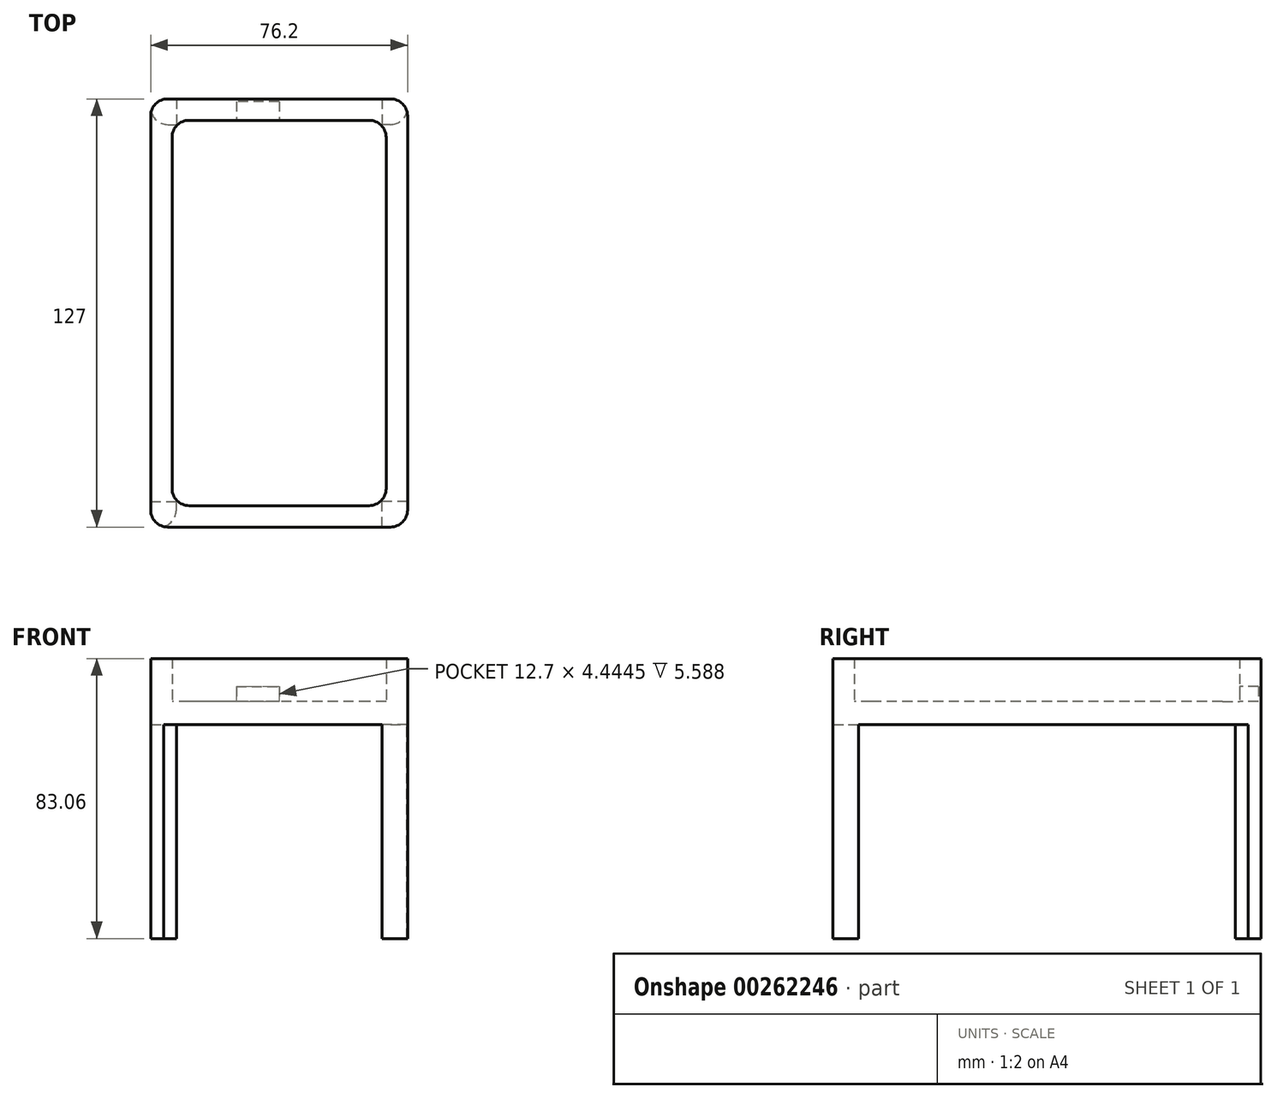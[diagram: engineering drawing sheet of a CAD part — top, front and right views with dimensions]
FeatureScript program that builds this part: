
annotation { "Feature Type Name" : "Feature", "Feature Type Description" : "" }
export const myFeature = defineFeature(function(context is Context, id is Id, definition is map)
    precondition{}
    {
        {
            var Q0;
            Q0=qCreatedBy(makeId("Top.planeOp"),FACE);
            var sketch = newSketch(context, id + "F0", { "sketchPlane" : qUnion([Q0])});
            skLineSegment(sketch, "E0.bottom", {"start": v(38.1, 63.5) * mm, "end": v(-38.1, 63.5) * mm});
            skLineSegment(sketch, "E0.top", {"start": v(38.1, -63.5) * mm, "end": v(-38.1, -63.5) * mm});
            skLineSegment(sketch, "E0.left", {"start": v(38.1, 63.5) * mm, "end": v(38.1, -63.5) * mm});
            skLineSegment(sketch, "E0.right", {"start": v(-38.1, 63.5) * mm, "end": v(-38.1, -63.5) * mm});
            skPoint(sketch, "E0.middle", {"position": v(0, 0) * mm});
            skLineSegment(sketch, "E1.bottom", {"start": v(31.75, 57.15) * mm, "end": v(-31.75, 57.15) * mm});
            skLineSegment(sketch, "E1.top", {"start": v(31.75, -57.15) * mm, "end": v(-31.75, -57.15) * mm});
            skLineSegment(sketch, "E1.left", {"start": v(31.75, 57.15) * mm, "end": v(31.75, -57.15) * mm});
            skLineSegment(sketch, "E1.right", {"start": v(-31.75, 57.15) * mm, "end": v(-31.75, -57.15) * mm});
            skSolve(sketch);
        }
        {
            var Q0;
            Q0 = qSketchRegion(id + "F0", true);
            extrude(context, id + "F1", {"entities" : qUnion([Q0]), "depth" : 12.7 * mm});
        }
        {
            var Q0;
            Q0=qCreatedBy(makeId("Top.planeOp"),FACE);
            var sketch = newSketch(context, id + "F2", { "sketchPlane" : qUnion([Q0])});
            skLineSegment(sketch, "E2.bottom", {"start": v(-38.1, 63.5) * mm, "end": v(38.1, 63.5) * mm});
            skLineSegment(sketch, "E2.top", {"start": v(-38.1, -63.5) * mm, "end": v(38.1, -63.5) * mm});
            skLineSegment(sketch, "E2.left", {"start": v(-38.1, 63.5) * mm, "end": v(-38.1, -63.5) * mm});
            skLineSegment(sketch, "E2.right", {"start": v(38.1, 63.5) * mm, "end": v(38.1, -63.5) * mm});
            skPoint(sketch, "E2.middle", {"position": v(0, 0) * mm});
            skSolve(sketch);
        }
        {
            var Q0;
            Q0 = qSketchRegion(id + "F2", true);
            extrude(context, id + "F3", {"entities" : qUnion([Q0]), "operationType" : NewBodyOperationType.ADD, "oppositeDirection" : true, "depth" : 6.86 * mm});
        }
        {
            var Q0;
            Q0=makeQuery(id+"F3.opExtrude","CAP_FACE",FACE,{"disambiguationData":[OSD([sQuery(id+"F2.wireOp",EDGE,"E2.bottom"),sQuery(id+"F2.wireOp",EDGE,"E2.top"),sQuery(id+"F2.wireOp",EDGE,"E2.left"),sQuery(id+"F2.wireOp",EDGE,"E2.right")])],"isStart":false});
            var sketch = newSketch(context, id + "F4", { "sketchPlane" : qUnion([Q0])});
            skLineSegment(sketch, "E3.bottom", {"start": v(38.1, -63.5) * mm, "end": v(30.48, -63.5) * mm});
            skLineSegment(sketch, "E3.top", {"start": v(38.1, -55.88) * mm, "end": v(30.48, -55.88) * mm});
            skLineSegment(sketch, "E3.left", {"start": v(38.1, -63.5) * mm, "end": v(38.1, -55.88) * mm});
            skLineSegment(sketch, "E3.right", {"start": v(30.48, -63.5) * mm, "end": v(30.48, -55.88) * mm});
            skLineSegment(sketch, "E4.MirrorCS", {"start": v(-38.1, -55.88) * mm, "end": v(-30.48, -55.88) * mm});
            skLineSegment(sketch, "E5.MirrorCS", {"start": v(-38.1, -63.5) * mm, "end": v(-38.1, -55.88) * mm});
            skLineSegment(sketch, "E6.MirrorCS", {"start": v(-38.1, -63.5) * mm, "end": v(-30.48, -63.5) * mm});
            skLineSegment(sketch, "E7.MirrorCS", {"start": v(-30.48, -63.5) * mm, "end": v(-30.48, -55.88) * mm});
            skLineSegment(sketch, "E8.MirrorCS", {"start": v(38.1, 55.88) * mm, "end": v(30.48, 55.88) * mm});
            skLineSegment(sketch, "E9.MirrorCS", {"start": v(30.48, 63.5) * mm, "end": v(30.48, 55.88) * mm});
            skLineSegment(sketch, "E10.MirrorCS", {"start": v(38.1, 63.5) * mm, "end": v(30.48, 63.5) * mm});
            skLineSegment(sketch, "E11.MirrorCS", {"start": v(38.1, 63.5) * mm, "end": v(38.1, 55.88) * mm});
            skLineSegment(sketch, "E12.MirrorCS", {"start": v(-30.48, 63.5) * mm, "end": v(-30.48, 55.88) * mm});
            skLineSegment(sketch, "E13.MirrorCS", {"start": v(-38.1, 55.88) * mm, "end": v(-30.48, 55.88) * mm});
            skLineSegment(sketch, "E14.MirrorCS", {"start": v(-38.1, 63.5) * mm, "end": v(-38.1, 55.88) * mm});
            skLineSegment(sketch, "E15.MirrorCS", {"start": v(-38.1, 63.5) * mm, "end": v(-30.48, 63.5) * mm});
            skSolve(sketch);
        }
        {
            var Q0;
            Q0=makeQuery(id+"F4.imprint","IMPRINT",FACE,{"disambiguationData":[TD([[makeQuery(id+"F4.imprint","IMPRINT",EDGE,{"derivedFrom":sQuery(id+"F4.wireOp",EDGE,"E3.bottom")}),1.0]])]});
            var Q1;
            Q1=makeQuery(id+"F4.imprint","IMPRINT",FACE,{"disambiguationData":[TD([[makeQuery(id+"F4.imprint","IMPRINT",EDGE,{"derivedFrom":sQuery(id+"F4.wireOp",EDGE,"E8.MirrorCS")}),-1.0]])]});
            var Q2;
            Q2=makeQuery(id+"F4.imprint","IMPRINT",FACE,{"disambiguationData":[TD([[makeQuery(id+"F4.imprint","IMPRINT",EDGE,{"derivedFrom":sQuery(id+"F4.wireOp",EDGE,"E12.MirrorCS")}),-1.0]])]});
            var Q3;
            Q3=makeQuery(id+"F4.imprint","IMPRINT",FACE,{"disambiguationData":[TD([[makeQuery(id+"F4.imprint","IMPRINT",EDGE,{"derivedFrom":sQuery(id+"F4.wireOp",EDGE,"E4.MirrorCS")}),-1.0]])]});
            extrude(context, id + "F5", {"entities" : qUnion([Q0, Q1, Q2, Q3]), "operationType" : NewBodyOperationType.ADD, "depth" : 63.5 * mm});
        }
        {
            var Q0;
            Q0=makeQuery(id+"F5.boolean.opBoolean","MERGE",EDGE,{"derivedFrom":[makeQuery(id+"F3.boolean.opBoolean","MERGE",EDGE,{"derivedFrom":[makeQuery(id+"F1.opExtrude","SWEPT_EDGE",EDGE,{"disambiguationData":[OSD([sQuery(id+"F0.wireOp",EDGE,"E0.top"),sQuery(id+"F0.wireOp",EDGE,"E0.left")])]}),makeQuery(id+"F3.opExtrude","SWEPT_EDGE",EDGE,{"disambiguationData":[OSD([sQuery(id+"F2.wireOp",EDGE,"E2.top"),sQuery(id+"F2.wireOp",EDGE,"E2.right")])]})]}),makeQuery(id+"F5.opExtrude","SWEPT_EDGE",EDGE,{"disambiguationData":[OSD([sQuery(id+"F4.wireOp",EDGE,"E10.MirrorCS"),sQuery(id+"F4.wireOp",EDGE,"E11.MirrorCS")])]})]});
            var Q1;
            Q1=makeQuery(id+"F5.boolean.opBoolean","MERGE",EDGE,{"derivedFrom":[makeQuery(id+"F3.boolean.opBoolean","MERGE",EDGE,{"derivedFrom":[makeQuery(id+"F1.opExtrude","SWEPT_EDGE",EDGE,{"disambiguationData":[OSD([sQuery(id+"F0.wireOp",EDGE,"E0.bottom"),sQuery(id+"F0.wireOp",EDGE,"E0.left")])]}),makeQuery(id+"F3.opExtrude","SWEPT_EDGE",EDGE,{"disambiguationData":[OSD([sQuery(id+"F2.wireOp",EDGE,"E2.bottom"),sQuery(id+"F2.wireOp",EDGE,"E2.right")])]})]}),makeQuery(id+"F5.opExtrude","SWEPT_EDGE",EDGE,{"disambiguationData":[OSD([sQuery(id+"F4.wireOp",EDGE,"E3.bottom"),sQuery(id+"F4.wireOp",EDGE,"E3.left")])]})]});
            var Q2;
            Q2=makeQuery(id+"F5.opExtrude","SWEPT_EDGE",EDGE,{"disambiguationData":[OSD([sQuery(id+"F2.wireOp",EDGE,"E2.right"),sQuery(id+"F4.wireOp",EDGE,"E3.top"),sQuery(id+"F4.wireOp",EDGE,"E3.left")])]});
            var Q3;
            Q3=makeQuery(id+"F5.opExtrude","SWEPT_EDGE",EDGE,{"disambiguationData":[OSD([sQuery(id+"F2.wireOp",EDGE,"E2.top"),sQuery(id+"F4.wireOp",EDGE,"E12.MirrorCS"),sQuery(id+"F4.wireOp",EDGE,"E15.MirrorCS")])]});
            var Q4;
            Q4=makeQuery(id+"F5.boolean.opBoolean","MERGE",EDGE,{"derivedFrom":[makeQuery(id+"F3.boolean.opBoolean","MERGE",EDGE,{"derivedFrom":[makeQuery(id+"F1.opExtrude","SWEPT_EDGE",EDGE,{"disambiguationData":[OSD([sQuery(id+"F0.wireOp",EDGE,"E0.top"),sQuery(id+"F0.wireOp",EDGE,"E0.right")])]}),makeQuery(id+"F3.opExtrude","SWEPT_EDGE",EDGE,{"disambiguationData":[OSD([sQuery(id+"F2.wireOp",EDGE,"E2.top"),sQuery(id+"F2.wireOp",EDGE,"E2.left")])]})]}),makeQuery(id+"F5.opExtrude","SWEPT_EDGE",EDGE,{"disambiguationData":[OSD([sQuery(id+"F4.wireOp",EDGE,"E14.MirrorCS"),sQuery(id+"F4.wireOp",EDGE,"E15.MirrorCS")])]})]});
            var Q5;
            Q5=makeQuery(id+"F5.boolean.opBoolean","MERGE",EDGE,{"derivedFrom":[makeQuery(id+"F3.boolean.opBoolean","MERGE",EDGE,{"derivedFrom":[makeQuery(id+"F1.opExtrude","SWEPT_EDGE",EDGE,{"disambiguationData":[OSD([sQuery(id+"F0.wireOp",EDGE,"E0.bottom"),sQuery(id+"F0.wireOp",EDGE,"E0.right")])]}),makeQuery(id+"F3.opExtrude","SWEPT_EDGE",EDGE,{"disambiguationData":[OSD([sQuery(id+"F2.wireOp",EDGE,"E2.bottom"),sQuery(id+"F2.wireOp",EDGE,"E2.left")])]})]}),makeQuery(id+"F5.opExtrude","SWEPT_EDGE",EDGE,{"disambiguationData":[OSD([sQuery(id+"F4.wireOp",EDGE,"E5.MirrorCS"),sQuery(id+"F4.wireOp",EDGE,"E6.MirrorCS")])]})]});
            var Q6;
            Q6=makeQuery(id+"F5.opExtrude","SWEPT_EDGE",EDGE,{"disambiguationData":[OSD([sQuery(id+"F2.wireOp",EDGE,"E2.left"),sQuery(id+"F4.wireOp",EDGE,"E4.MirrorCS"),sQuery(id+"F4.wireOp",EDGE,"E5.MirrorCS")])]});
            fillet(context, id + "F6", {"entities" : qUnion([Q0, Q1, Q2, Q3, Q4, Q5, Q6]), "radius" : 5.08 * mm, "tangentPropagation" : true, "allowEdgeOverflow" : false});
        }
        {
            var Q0;
            Q0=makeQuery(id+"F1.opExtrude","SWEPT_EDGE",EDGE,{"disambiguationData":[OSD([sQuery(id+"F0.wireOp",EDGE,"E1.top"),sQuery(id+"F0.wireOp",EDGE,"E1.right")])]});
            var Q1;
            Q1=makeQuery(id+"F1.opExtrude","SWEPT_EDGE",EDGE,{"disambiguationData":[OSD([sQuery(id+"F0.wireOp",EDGE,"E1.top"),sQuery(id+"F0.wireOp",EDGE,"E1.left")])]});
            var Q2;
            Q2=makeQuery(id+"F1.opExtrude","SWEPT_EDGE",EDGE,{"disambiguationData":[OSD([sQuery(id+"F0.wireOp",EDGE,"E1.bottom"),sQuery(id+"F0.wireOp",EDGE,"E1.right")])]});
            var Q3;
            Q3=makeQuery(id+"F1.opExtrude","SWEPT_EDGE",EDGE,{"disambiguationData":[OSD([sQuery(id+"F0.wireOp",EDGE,"E1.bottom"),sQuery(id+"F0.wireOp",EDGE,"E1.left")])]});
            fillet(context, id + "F7", {"entities" : qUnion([Q0, Q1, Q2, Q3]), "radius" : 5.08 * mm, "tangentPropagation" : true, "allowEdgeOverflow" : false});
        }
        {
            var Q0;
            Q0=makeQuery(id+"F1.opExtrude","SWEPT_FACE",FACE,{"disambiguationData":[OSD([sQuery(id+"F0.wireOp",EDGE,"E1.bottom")])]});
            var sketch = newSketch(context, id + "F8", { "sketchPlane" : qUnion([Q0])});
            skLineSegment(sketch, "E16.bottom", {"start": v(-12.7, 4.44) * mm, "end": v(0, 4.44) * mm});
            skLineSegment(sketch, "E16.top", {"start": v(-12.7, 0) * mm, "end": v(0, 0) * mm});
            skLineSegment(sketch, "E16.left", {"start": v(-12.7, 4.44) * mm, "end": v(-12.7, 0) * mm});
            skLineSegment(sketch, "E16.right", {"start": v(0, 4.44) * mm, "end": v(0, 0) * mm});
            skSolve(sketch);
        }
        {
            var Q0;
            Q0 = qSketchRegion(id + "F8", true);
            extrude(context, id + "F9", {"entities" : qUnion([Q0]), "operationType" : NewBodyOperationType.REMOVE, "oppositeDirection" : true, "depth" : 5.6 * mm});
        }
    });
